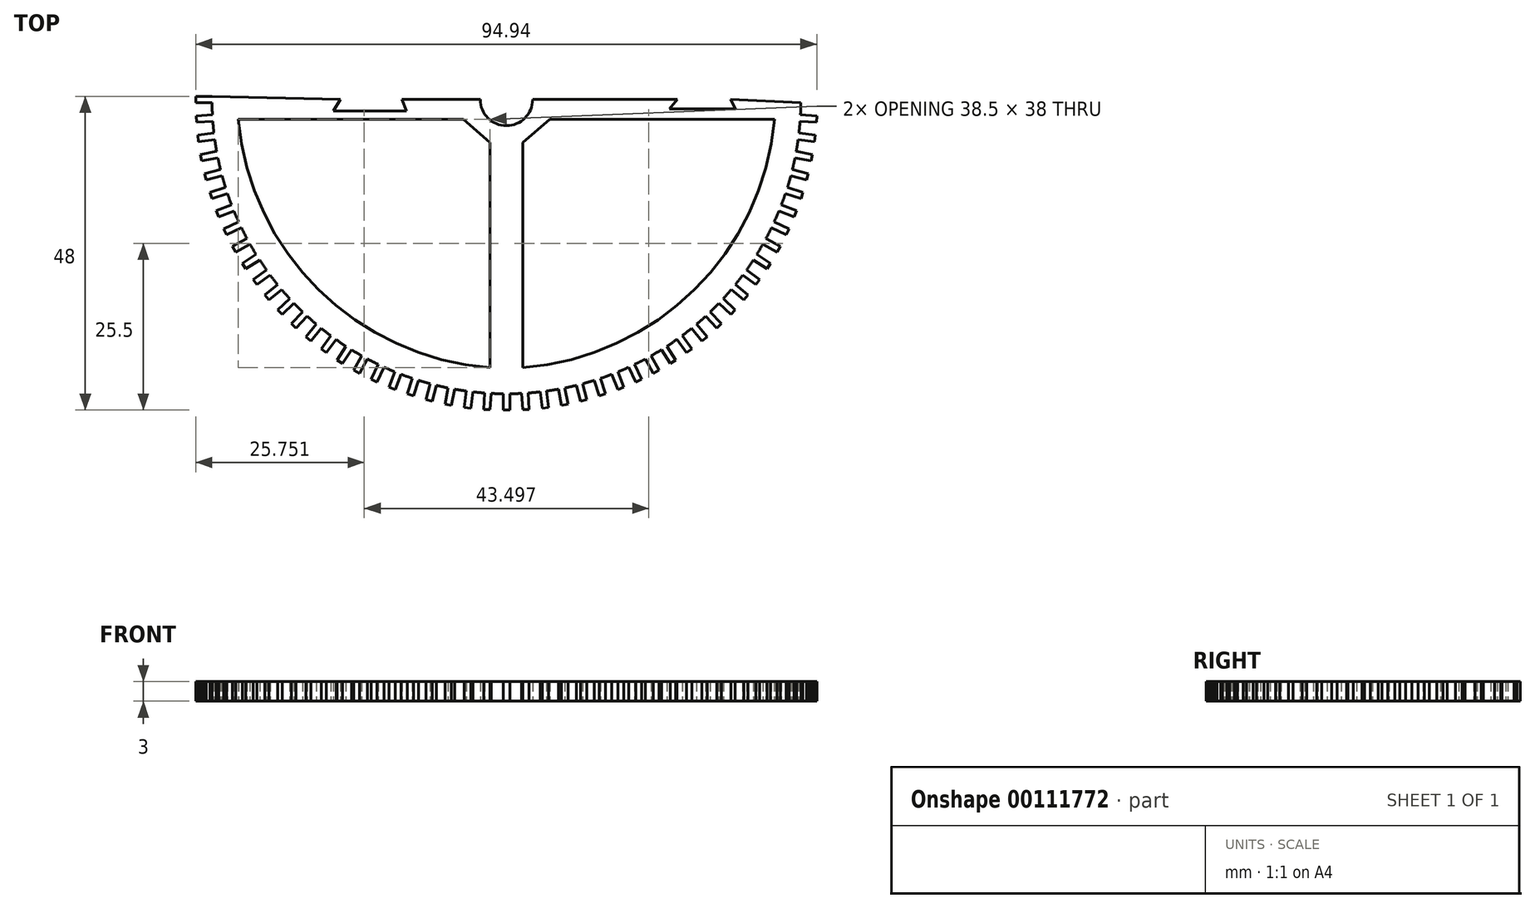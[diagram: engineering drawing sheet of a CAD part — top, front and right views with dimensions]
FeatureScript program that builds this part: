
annotation { "Feature Type Name" : "Feature", "Feature Type Description" : "" }
export const myFeature = defineFeature(function(context is Context, id is Id, definition is map)
    precondition{}
    {
        {
            var Q0;
            Q0=qCreatedBy(makeId("Top.planeOp"),FACE);
            var sketch = newSketch(context, id + "F0", { "sketchPlane" : qUnion([Q0])});
            skArc(sketch, "E0", {"start": v(-45, 0.5) * mm, "mid": v(-0.5, -45) * mm, "end": v(45, -0.5) * mm});
            skLineSegment(sketch, "E1.2.25.0", {"start": v(-47.5, 0.5) * mm, "end": v(-45, 0.5) * mm});
            skLineSegment(sketch, "E1.3.25.0", {"start": v(-47.5, -0.5) * mm, "end": v(-45, -0.5) * mm});
            skLineSegment(sketch, "E1.6.25.0", {"start": v(-47.5, 0) * mm, "end": v(-47.5, -0.5) * mm});
            skLineSegment(sketch, "E1.9.25.0", {"start": v(-47.5, 0) * mm, "end": v(-47.5, 0.5) * mm});
            skLineSegment(sketch, "E1.2.26.0", {"start": v(-47.44, -2.48) * mm, "end": v(-44.94, -2.33) * mm});
            skLineSegment(sketch, "E1.3.26.0", {"start": v(-47.37, -3.48) * mm, "end": v(-44.88, -3.32) * mm});
            skLineSegment(sketch, "E1.6.26.0", {"start": v(-47.4, -2.98) * mm, "end": v(-47.37, -3.48) * mm});
            skLineSegment(sketch, "E1.9.26.0", {"start": v(-47.4, -2.98) * mm, "end": v(-47.44, -2.48) * mm});
            skLineSegment(sketch, "E1.2.27.0", {"start": v(-47.19, -5.46) * mm, "end": v(-44.7, -5.14) * mm});
            skLineSegment(sketch, "E1.3.27.0", {"start": v(-47.06, -6.45) * mm, "end": v(-44.58, -6.14) * mm});
            skLineSegment(sketch, "E1.6.27.0", {"start": v(-47.13, -5.95) * mm, "end": v(-47.06, -6.45) * mm});
            skLineSegment(sketch, "E1.9.27.0", {"start": v(-47.13, -5.95) * mm, "end": v(-47.19, -5.46) * mm});
            skLineSegment(sketch, "E1.2.28.0", {"start": v(-46.75, -8.4) * mm, "end": v(-44.3, -7.94) * mm});
            skLineSegment(sketch, "E1.3.28.0", {"start": v(-46.56, -9.4) * mm, "end": v(-44.1, -8.92) * mm});
            skLineSegment(sketch, "E1.6.28.0", {"start": v(-46.66, -8.9) * mm, "end": v(-46.56, -9.4) * mm});
            skLineSegment(sketch, "E1.9.28.0", {"start": v(-46.66, -8.9) * mm, "end": v(-46.75, -8.4) * mm});
            skLineSegment(sketch, "E1.2.29.0", {"start": v(-46.13, -11.33) * mm, "end": v(-43.7, -10.7) * mm});
            skLineSegment(sketch, "E1.3.29.0", {"start": v(-45.88, -12.3) * mm, "end": v(-43.46, -11.67) * mm});
            skLineSegment(sketch, "E1.6.29.0", {"start": v(-46, -11.81) * mm, "end": v(-45.88, -12.3) * mm});
            skLineSegment(sketch, "E1.9.29.0", {"start": v(-46, -11.81) * mm, "end": v(-46.13, -11.33) * mm});
            skLineSegment(sketch, "E1.2.30.0", {"start": v(-45.33, -14.2) * mm, "end": v(-42.95, -13.43) * mm});
            skLineSegment(sketch, "E1.3.30.0", {"start": v(-45.02, -15.15) * mm, "end": v(-42.64, -14.38) * mm});
            skLineSegment(sketch, "E1.6.30.0", {"start": v(-45.18, -14.68) * mm, "end": v(-45.02, -15.15) * mm});
            skLineSegment(sketch, "E1.9.30.0", {"start": v(-45.18, -14.68) * mm, "end": v(-45.33, -14.2) * mm});
            skLineSegment(sketch, "E1.2.31.0", {"start": v(-44.35, -17.02) * mm, "end": v(-42.02, -16.1) * mm});
            skLineSegment(sketch, "E1.3.31.0", {"start": v(-43.98, -17.95) * mm, "end": v(-41.65, -17.03) * mm});
            skLineSegment(sketch, "E1.6.31.0", {"start": v(-44.16, -17.49) * mm, "end": v(-43.98, -17.95) * mm});
            skLineSegment(sketch, "E1.9.31.0", {"start": v(-44.16, -17.49) * mm, "end": v(-44.35, -17.02) * mm});
            skLineSegment(sketch, "E1.2.32.0", {"start": v(-43.2, -19.77) * mm, "end": v(-40.93, -18.7) * mm});
            skLineSegment(sketch, "E1.3.32.0", {"start": v(-42.77, -20.68) * mm, "end": v(-40.5, -19.61) * mm});
            skLineSegment(sketch, "E1.6.32.0", {"start": v(-42.98, -20.22) * mm, "end": v(-42.77, -20.68) * mm});
            skLineSegment(sketch, "E1.9.32.0", {"start": v(-42.98, -20.22) * mm, "end": v(-43.2, -19.77) * mm});
            skLineSegment(sketch, "E1.2.33.0", {"start": v(-41.87, -22.45) * mm, "end": v(-39.67, -21.24) * mm});
            skLineSegment(sketch, "E1.3.33.0", {"start": v(-41.38, -23.32) * mm, "end": v(-39.2, -22.12) * mm});
            skLineSegment(sketch, "E1.6.33.0", {"start": v(-41.62, -22.88) * mm, "end": v(-41.38, -23.32) * mm});
            skLineSegment(sketch, "E1.9.33.0", {"start": v(-41.62, -22.88) * mm, "end": v(-41.87, -22.45) * mm});
            skLineSegment(sketch, "E1.2.34.0", {"start": v(-40.37, -25.03) * mm, "end": v(-38.26, -23.69) * mm});
            skLineSegment(sketch, "E1.3.34.0", {"start": v(-39.84, -25.87) * mm, "end": v(-37.72, -24.53) * mm});
            skLineSegment(sketch, "E1.6.34.0", {"start": v(-40.1, -25.45) * mm, "end": v(-39.84, -25.87) * mm});
            skLineSegment(sketch, "E1.9.34.0", {"start": v(-40.1, -25.45) * mm, "end": v(-40.37, -25.03) * mm});
            skLineSegment(sketch, "E1.2.35.0", {"start": v(-38.72, -27.52) * mm, "end": v(-36.7, -26.04) * mm});
            skLineSegment(sketch, "E1.3.35.0", {"start": v(-38.13, -28.32) * mm, "end": v(-36.1, -26.85) * mm});
            skLineSegment(sketch, "E1.6.35.0", {"start": v(-38.43, -27.92) * mm, "end": v(-38.13, -28.32) * mm});
            skLineSegment(sketch, "E1.9.35.0", {"start": v(-38.43, -27.92) * mm, "end": v(-38.72, -27.52) * mm});
            skLineSegment(sketch, "E1.2.36.0", {"start": v(-36.92, -29.9) * mm, "end": v(-34.99, -28.3) * mm});
            skLineSegment(sketch, "E1.3.36.0", {"start": v(-36.28, -30.66) * mm, "end": v(-34.35, -29.07) * mm});
            skLineSegment(sketch, "E1.6.36.0", {"start": v(-36.6, -30.28) * mm, "end": v(-36.28, -30.66) * mm});
            skLineSegment(sketch, "E1.9.36.0", {"start": v(-36.6, -30.28) * mm, "end": v(-36.92, -29.9) * mm});
            skLineSegment(sketch, "E1.2.37.0", {"start": v(-34.97, -32.15) * mm, "end": v(-33.14, -30.44) * mm});
            skLineSegment(sketch, "E1.3.37.0", {"start": v(-34.28, -32.88) * mm, "end": v(-32.46, -31.17) * mm});
            skLineSegment(sketch, "E1.6.37.0", {"start": v(-34.63, -32.52) * mm, "end": v(-34.28, -32.88) * mm});
            skLineSegment(sketch, "E1.9.37.0", {"start": v(-34.63, -32.52) * mm, "end": v(-34.97, -32.15) * mm});
            skLineSegment(sketch, "E1.2.38.0", {"start": v(-32.88, -34.28) * mm, "end": v(-31.17, -32.46) * mm});
            skLineSegment(sketch, "E1.3.38.0", {"start": v(-32.15, -34.97) * mm, "end": v(-30.44, -33.14) * mm});
            skLineSegment(sketch, "E1.6.38.0", {"start": v(-32.52, -34.63) * mm, "end": v(-32.15, -34.97) * mm});
            skLineSegment(sketch, "E1.9.38.0", {"start": v(-32.52, -34.63) * mm, "end": v(-32.88, -34.28) * mm});
            skLineSegment(sketch, "E1.2.39.0", {"start": v(-30.66, -36.28) * mm, "end": v(-29.07, -34.35) * mm});
            skLineSegment(sketch, "E1.3.39.0", {"start": v(-29.9, -36.92) * mm, "end": v(-28.3, -34.99) * mm});
            skLineSegment(sketch, "E1.6.39.0", {"start": v(-30.28, -36.6) * mm, "end": v(-29.9, -36.92) * mm});
            skLineSegment(sketch, "E1.9.39.0", {"start": v(-30.28, -36.6) * mm, "end": v(-30.66, -36.28) * mm});
            skLineSegment(sketch, "E1.2.40.0", {"start": v(-28.32, -38.13) * mm, "end": v(-26.85, -36.1) * mm});
            skLineSegment(sketch, "E1.3.40.0", {"start": v(-27.52, -38.72) * mm, "end": v(-26.04, -36.7) * mm});
            skLineSegment(sketch, "E1.6.40.0", {"start": v(-27.92, -38.43) * mm, "end": v(-27.52, -38.72) * mm});
            skLineSegment(sketch, "E1.9.40.0", {"start": v(-27.92, -38.43) * mm, "end": v(-28.32, -38.13) * mm});
            skLineSegment(sketch, "E1.2.41.0", {"start": v(-25.87, -39.84) * mm, "end": v(-24.53, -37.72) * mm});
            skLineSegment(sketch, "E1.3.41.0", {"start": v(-25.03, -40.37) * mm, "end": v(-23.69, -38.26) * mm});
            skLineSegment(sketch, "E1.6.41.0", {"start": v(-25.45, -40.1) * mm, "end": v(-25.03, -40.37) * mm});
            skLineSegment(sketch, "E1.9.41.0", {"start": v(-25.45, -40.1) * mm, "end": v(-25.87, -39.84) * mm});
            skLineSegment(sketch, "E1.2.42.0", {"start": v(-23.32, -41.38) * mm, "end": v(-22.12, -39.2) * mm});
            skLineSegment(sketch, "E1.3.42.0", {"start": v(-22.45, -41.87) * mm, "end": v(-21.24, -39.67) * mm});
            skLineSegment(sketch, "E1.6.42.0", {"start": v(-22.88, -41.62) * mm, "end": v(-22.45, -41.87) * mm});
            skLineSegment(sketch, "E1.9.42.0", {"start": v(-22.88, -41.62) * mm, "end": v(-23.32, -41.38) * mm});
            skLineSegment(sketch, "E1.2.43.0", {"start": v(-20.68, -42.77) * mm, "end": v(-19.61, -40.5) * mm});
            skLineSegment(sketch, "E1.3.43.0", {"start": v(-19.77, -43.2) * mm, "end": v(-18.7, -40.93) * mm});
            skLineSegment(sketch, "E1.6.43.0", {"start": v(-20.22, -42.98) * mm, "end": v(-19.77, -43.2) * mm});
            skLineSegment(sketch, "E1.9.43.0", {"start": v(-20.22, -42.98) * mm, "end": v(-20.68, -42.77) * mm});
            skLineSegment(sketch, "E1.2.44.0", {"start": v(-17.95, -43.98) * mm, "end": v(-17.03, -41.65) * mm});
            skLineSegment(sketch, "E1.3.44.0", {"start": v(-17.02, -44.35) * mm, "end": v(-16.1, -42.02) * mm});
            skLineSegment(sketch, "E1.6.44.0", {"start": v(-17.49, -44.16) * mm, "end": v(-17.02, -44.35) * mm});
            skLineSegment(sketch, "E1.9.44.0", {"start": v(-17.49, -44.16) * mm, "end": v(-17.95, -43.98) * mm});
            skLineSegment(sketch, "E1.2.45.0", {"start": v(-15.15, -45.02) * mm, "end": v(-14.38, -42.64) * mm});
            skLineSegment(sketch, "E1.3.45.0", {"start": v(-14.2, -45.33) * mm, "end": v(-13.43, -42.95) * mm});
            skLineSegment(sketch, "E1.6.45.0", {"start": v(-14.68, -45.18) * mm, "end": v(-14.2, -45.33) * mm});
            skLineSegment(sketch, "E1.9.45.0", {"start": v(-14.68, -45.18) * mm, "end": v(-15.15, -45.02) * mm});
            skLineSegment(sketch, "E1.2.46.0", {"start": v(-12.3, -45.88) * mm, "end": v(-11.67, -43.46) * mm});
            skLineSegment(sketch, "E1.3.46.0", {"start": v(-11.33, -46.13) * mm, "end": v(-10.7, -43.7) * mm});
            skLineSegment(sketch, "E1.6.46.0", {"start": v(-11.81, -46) * mm, "end": v(-11.33, -46.13) * mm});
            skLineSegment(sketch, "E1.9.46.0", {"start": v(-11.81, -46) * mm, "end": v(-12.3, -45.88) * mm});
            skLineSegment(sketch, "E1.2.47.0", {"start": v(-9.4, -46.56) * mm, "end": v(-8.92, -44.1) * mm});
            skLineSegment(sketch, "E1.3.47.0", {"start": v(-8.4, -46.75) * mm, "end": v(-7.94, -44.3) * mm});
            skLineSegment(sketch, "E1.6.47.0", {"start": v(-8.9, -46.66) * mm, "end": v(-8.4, -46.75) * mm});
            skLineSegment(sketch, "E1.9.47.0", {"start": v(-8.9, -46.66) * mm, "end": v(-9.4, -46.56) * mm});
            skLineSegment(sketch, "E1.2.48.0", {"start": v(-6.45, -47.06) * mm, "end": v(-6.14, -44.58) * mm});
            skLineSegment(sketch, "E1.3.48.0", {"start": v(-5.46, -47.19) * mm, "end": v(-5.14, -44.7) * mm});
            skLineSegment(sketch, "E1.6.48.0", {"start": v(-5.95, -47.13) * mm, "end": v(-5.46, -47.19) * mm});
            skLineSegment(sketch, "E1.9.48.0", {"start": v(-5.95, -47.13) * mm, "end": v(-6.45, -47.06) * mm});
            skLineSegment(sketch, "E1.2.49.0", {"start": v(-3.48, -47.37) * mm, "end": v(-3.32, -44.88) * mm});
            skLineSegment(sketch, "E1.3.49.0", {"start": v(-2.48, -47.44) * mm, "end": v(-2.33, -44.94) * mm});
            skLineSegment(sketch, "E1.6.49.0", {"start": v(-2.98, -47.4) * mm, "end": v(-2.48, -47.44) * mm});
            skLineSegment(sketch, "E1.9.49.0", {"start": v(-2.98, -47.4) * mm, "end": v(-3.48, -47.37) * mm});
            skLineSegment(sketch, "E1.2.50.0", {"start": v(-0.5, -47.5) * mm, "end": v(-0.5, -45) * mm});
            skLineSegment(sketch, "E1.3.50.0", {"start": v(0.5, -47.5) * mm, "end": v(0.5, -45) * mm});
            skLineSegment(sketch, "E1.6.50.0", {"start": v(0, -47.5) * mm, "end": v(0.5, -47.5) * mm});
            skLineSegment(sketch, "E1.9.50.0", {"start": v(0, -47.5) * mm, "end": v(-0.5, -47.5) * mm});
            skLineSegment(sketch, "E1.2.51.0", {"start": v(2.48, -47.44) * mm, "end": v(2.33, -44.94) * mm});
            skLineSegment(sketch, "E1.3.51.0", {"start": v(3.48, -47.37) * mm, "end": v(3.32, -44.88) * mm});
            skLineSegment(sketch, "E1.6.51.0", {"start": v(2.98, -47.4) * mm, "end": v(3.48, -47.37) * mm});
            skLineSegment(sketch, "E1.9.51.0", {"start": v(2.98, -47.4) * mm, "end": v(2.48, -47.44) * mm});
            skLineSegment(sketch, "E1.2.52.0", {"start": v(5.46, -47.19) * mm, "end": v(5.14, -44.7) * mm});
            skLineSegment(sketch, "E1.3.52.0", {"start": v(6.45, -47.06) * mm, "end": v(6.14, -44.58) * mm});
            skLineSegment(sketch, "E1.6.52.0", {"start": v(5.95, -47.13) * mm, "end": v(6.45, -47.06) * mm});
            skLineSegment(sketch, "E1.9.52.0", {"start": v(5.95, -47.13) * mm, "end": v(5.46, -47.19) * mm});
            skLineSegment(sketch, "E1.2.53.0", {"start": v(8.4, -46.75) * mm, "end": v(7.94, -44.3) * mm});
            skLineSegment(sketch, "E1.3.53.0", {"start": v(9.4, -46.56) * mm, "end": v(8.92, -44.1) * mm});
            skLineSegment(sketch, "E1.6.53.0", {"start": v(8.9, -46.66) * mm, "end": v(9.4, -46.56) * mm});
            skLineSegment(sketch, "E1.9.53.0", {"start": v(8.9, -46.66) * mm, "end": v(8.4, -46.75) * mm});
            skLineSegment(sketch, "E1.2.54.0", {"start": v(11.33, -46.13) * mm, "end": v(10.7, -43.7) * mm});
            skLineSegment(sketch, "E1.3.54.0", {"start": v(12.3, -45.88) * mm, "end": v(11.67, -43.46) * mm});
            skLineSegment(sketch, "E1.6.54.0", {"start": v(11.81, -46) * mm, "end": v(12.3, -45.88) * mm});
            skLineSegment(sketch, "E1.9.54.0", {"start": v(11.81, -46) * mm, "end": v(11.33, -46.13) * mm});
            skLineSegment(sketch, "E1.2.55.0", {"start": v(14.2, -45.33) * mm, "end": v(13.43, -42.95) * mm});
            skLineSegment(sketch, "E1.3.55.0", {"start": v(15.15, -45.02) * mm, "end": v(14.38, -42.64) * mm});
            skLineSegment(sketch, "E1.6.55.0", {"start": v(14.68, -45.18) * mm, "end": v(15.15, -45.02) * mm});
            skLineSegment(sketch, "E1.9.55.0", {"start": v(14.68, -45.18) * mm, "end": v(14.2, -45.33) * mm});
            skLineSegment(sketch, "E1.2.56.0", {"start": v(17.02, -44.35) * mm, "end": v(16.1, -42.02) * mm});
            skLineSegment(sketch, "E1.3.56.0", {"start": v(17.95, -43.98) * mm, "end": v(17.03, -41.65) * mm});
            skLineSegment(sketch, "E1.6.56.0", {"start": v(17.49, -44.16) * mm, "end": v(17.95, -43.98) * mm});
            skLineSegment(sketch, "E1.9.56.0", {"start": v(17.49, -44.16) * mm, "end": v(17.02, -44.35) * mm});
            skLineSegment(sketch, "E1.2.57.0", {"start": v(19.77, -43.2) * mm, "end": v(18.7, -40.93) * mm});
            skLineSegment(sketch, "E1.3.57.0", {"start": v(20.68, -42.77) * mm, "end": v(19.61, -40.5) * mm});
            skLineSegment(sketch, "E1.6.57.0", {"start": v(20.22, -42.98) * mm, "end": v(20.68, -42.77) * mm});
            skLineSegment(sketch, "E1.9.57.0", {"start": v(20.22, -42.98) * mm, "end": v(19.77, -43.2) * mm});
            skLineSegment(sketch, "E1.2.58.0", {"start": v(22.45, -41.87) * mm, "end": v(21.24, -39.67) * mm});
            skLineSegment(sketch, "E1.3.58.0", {"start": v(23.32, -41.38) * mm, "end": v(22.12, -39.2) * mm});
            skLineSegment(sketch, "E1.6.58.0", {"start": v(22.88, -41.62) * mm, "end": v(23.32, -41.38) * mm});
            skLineSegment(sketch, "E1.9.58.0", {"start": v(22.88, -41.62) * mm, "end": v(22.45, -41.87) * mm});
            skLineSegment(sketch, "E1.2.59.0", {"start": v(25.03, -40.37) * mm, "end": v(23.69, -38.26) * mm});
            skLineSegment(sketch, "E1.3.59.0", {"start": v(25.87, -39.84) * mm, "end": v(24.53, -37.72) * mm});
            skLineSegment(sketch, "E1.6.59.0", {"start": v(25.45, -40.1) * mm, "end": v(25.87, -39.84) * mm});
            skLineSegment(sketch, "E1.9.59.0", {"start": v(25.45, -40.1) * mm, "end": v(25.03, -40.37) * mm});
            skLineSegment(sketch, "E1.2.60.0", {"start": v(27.52, -38.72) * mm, "end": v(26.04, -36.7) * mm});
            skLineSegment(sketch, "E1.3.60.0", {"start": v(28.32, -38.13) * mm, "end": v(26.85, -36.1) * mm});
            skLineSegment(sketch, "E1.6.60.0", {"start": v(27.92, -38.43) * mm, "end": v(28.32, -38.13) * mm});
            skLineSegment(sketch, "E1.9.60.0", {"start": v(27.92, -38.43) * mm, "end": v(27.52, -38.72) * mm});
            skLineSegment(sketch, "E1.2.61.0", {"start": v(29.9, -36.92) * mm, "end": v(28.3, -34.99) * mm});
            skLineSegment(sketch, "E1.3.61.0", {"start": v(30.66, -36.28) * mm, "end": v(29.07, -34.35) * mm});
            skLineSegment(sketch, "E1.6.61.0", {"start": v(30.28, -36.6) * mm, "end": v(30.66, -36.28) * mm});
            skLineSegment(sketch, "E1.9.61.0", {"start": v(30.28, -36.6) * mm, "end": v(29.9, -36.92) * mm});
            skLineSegment(sketch, "E1.2.62.0", {"start": v(32.15, -34.97) * mm, "end": v(30.44, -33.14) * mm});
            skLineSegment(sketch, "E1.3.62.0", {"start": v(32.88, -34.28) * mm, "end": v(31.17, -32.46) * mm});
            skLineSegment(sketch, "E1.6.62.0", {"start": v(32.52, -34.63) * mm, "end": v(32.88, -34.28) * mm});
            skLineSegment(sketch, "E1.9.62.0", {"start": v(32.52, -34.63) * mm, "end": v(32.15, -34.97) * mm});
            skLineSegment(sketch, "E1.2.63.0", {"start": v(34.28, -32.88) * mm, "end": v(32.46, -31.17) * mm});
            skLineSegment(sketch, "E1.3.63.0", {"start": v(34.97, -32.15) * mm, "end": v(33.14, -30.44) * mm});
            skLineSegment(sketch, "E1.6.63.0", {"start": v(34.63, -32.52) * mm, "end": v(34.97, -32.15) * mm});
            skLineSegment(sketch, "E1.9.63.0", {"start": v(34.63, -32.52) * mm, "end": v(34.28, -32.88) * mm});
            skLineSegment(sketch, "E1.2.64.0", {"start": v(36.28, -30.66) * mm, "end": v(34.35, -29.07) * mm});
            skLineSegment(sketch, "E1.3.64.0", {"start": v(36.92, -29.9) * mm, "end": v(34.99, -28.3) * mm});
            skLineSegment(sketch, "E1.6.64.0", {"start": v(36.6, -30.28) * mm, "end": v(36.92, -29.9) * mm});
            skLineSegment(sketch, "E1.9.64.0", {"start": v(36.6, -30.28) * mm, "end": v(36.28, -30.66) * mm});
            skLineSegment(sketch, "E1.2.65.0", {"start": v(38.13, -28.32) * mm, "end": v(36.1, -26.85) * mm});
            skLineSegment(sketch, "E1.3.65.0", {"start": v(38.72, -27.52) * mm, "end": v(36.7, -26.04) * mm});
            skLineSegment(sketch, "E1.6.65.0", {"start": v(38.43, -27.92) * mm, "end": v(38.72, -27.52) * mm});
            skLineSegment(sketch, "E1.9.65.0", {"start": v(38.43, -27.92) * mm, "end": v(38.13, -28.32) * mm});
            skLineSegment(sketch, "E1.2.66.0", {"start": v(39.84, -25.87) * mm, "end": v(37.72, -24.53) * mm});
            skLineSegment(sketch, "E1.3.66.0", {"start": v(40.37, -25.03) * mm, "end": v(38.26, -23.69) * mm});
            skLineSegment(sketch, "E1.6.66.0", {"start": v(40.1, -25.45) * mm, "end": v(40.37, -25.03) * mm});
            skLineSegment(sketch, "E1.9.66.0", {"start": v(40.1, -25.45) * mm, "end": v(39.84, -25.87) * mm});
            skLineSegment(sketch, "E1.2.67.0", {"start": v(41.38, -23.32) * mm, "end": v(39.2, -22.12) * mm});
            skLineSegment(sketch, "E1.3.67.0", {"start": v(41.87, -22.45) * mm, "end": v(39.67, -21.24) * mm});
            skLineSegment(sketch, "E1.6.67.0", {"start": v(41.62, -22.88) * mm, "end": v(41.87, -22.45) * mm});
            skLineSegment(sketch, "E1.9.67.0", {"start": v(41.62, -22.88) * mm, "end": v(41.38, -23.32) * mm});
            skLineSegment(sketch, "E1.2.68.0", {"start": v(42.77, -20.68) * mm, "end": v(40.5, -19.61) * mm});
            skLineSegment(sketch, "E1.3.68.0", {"start": v(43.2, -19.77) * mm, "end": v(40.93, -18.7) * mm});
            skLineSegment(sketch, "E1.6.68.0", {"start": v(42.98, -20.22) * mm, "end": v(43.2, -19.77) * mm});
            skLineSegment(sketch, "E1.9.68.0", {"start": v(42.98, -20.22) * mm, "end": v(42.77, -20.68) * mm});
            skLineSegment(sketch, "E1.2.69.0", {"start": v(43.98, -17.95) * mm, "end": v(41.65, -17.03) * mm});
            skLineSegment(sketch, "E1.3.69.0", {"start": v(44.35, -17.02) * mm, "end": v(42.02, -16.1) * mm});
            skLineSegment(sketch, "E1.6.69.0", {"start": v(44.16, -17.49) * mm, "end": v(44.35, -17.02) * mm});
            skLineSegment(sketch, "E1.9.69.0", {"start": v(44.16, -17.49) * mm, "end": v(43.98, -17.95) * mm});
            skLineSegment(sketch, "E1.2.70.0", {"start": v(45.02, -15.15) * mm, "end": v(42.64, -14.38) * mm});
            skLineSegment(sketch, "E1.3.70.0", {"start": v(45.33, -14.2) * mm, "end": v(42.95, -13.43) * mm});
            skLineSegment(sketch, "E1.6.70.0", {"start": v(45.18, -14.68) * mm, "end": v(45.33, -14.2) * mm});
            skLineSegment(sketch, "E1.9.70.0", {"start": v(45.18, -14.68) * mm, "end": v(45.02, -15.15) * mm});
            skLineSegment(sketch, "E1.2.71.0", {"start": v(45.88, -12.3) * mm, "end": v(43.46, -11.67) * mm});
            skLineSegment(sketch, "E1.3.71.0", {"start": v(46.13, -11.33) * mm, "end": v(43.7, -10.7) * mm});
            skLineSegment(sketch, "E1.6.71.0", {"start": v(46, -11.81) * mm, "end": v(46.13, -11.33) * mm});
            skLineSegment(sketch, "E1.9.71.0", {"start": v(46, -11.81) * mm, "end": v(45.88, -12.3) * mm});
            skLineSegment(sketch, "E1.2.72.0", {"start": v(46.56, -9.4) * mm, "end": v(44.1, -8.92) * mm});
            skLineSegment(sketch, "E1.3.72.0", {"start": v(46.75, -8.4) * mm, "end": v(44.3, -7.94) * mm});
            skLineSegment(sketch, "E1.6.72.0", {"start": v(46.66, -8.9) * mm, "end": v(46.75, -8.4) * mm});
            skLineSegment(sketch, "E1.9.72.0", {"start": v(46.66, -8.9) * mm, "end": v(46.56, -9.4) * mm});
            skLineSegment(sketch, "E1.2.73.0", {"start": v(47.06, -6.45) * mm, "end": v(44.58, -6.14) * mm});
            skLineSegment(sketch, "E1.3.73.0", {"start": v(47.19, -5.46) * mm, "end": v(44.7, -5.14) * mm});
            skLineSegment(sketch, "E1.6.73.0", {"start": v(47.13, -5.95) * mm, "end": v(47.19, -5.46) * mm});
            skLineSegment(sketch, "E1.9.73.0", {"start": v(47.13, -5.95) * mm, "end": v(47.06, -6.45) * mm});
            skLineSegment(sketch, "E1.2.74.0", {"start": v(47.37, -3.48) * mm, "end": v(44.88, -3.32) * mm});
            skLineSegment(sketch, "E1.3.74.0", {"start": v(47.44, -2.48) * mm, "end": v(44.94, -2.33) * mm});
            skLineSegment(sketch, "E1.6.74.0", {"start": v(47.4, -2.98) * mm, "end": v(47.44, -2.48) * mm});
            skLineSegment(sketch, "E1.9.74.0", {"start": v(47.4, -2.98) * mm, "end": v(47.37, -3.48) * mm});
            skLineSegment(sketch, "E2.MirrorCS", {"start": v(-6.6, -3) * mm, "end": v(-41, -3) * mm});
            skLineSegment(sketch, "E3.MirrorCS", {"start": v(-2.5, -6.6) * mm, "end": v(-6.6, -3) * mm});
            skLineSegment(sketch, "E4.MirrorCS", {"start": v(-2.5, -6.6) * mm, "end": v(-2.5, -41) * mm});
            skArc(sketch, "E5.MirrorCS", {"start": v(-41, -3) * mm, "mid": v(-28.72, -29.07) * mm, "end": v(-2.5, -41) * mm});
            skLineSegment(sketch, "E6.MirrorCS", {"start": v(2.5, -6.6) * mm, "end": v(2.5, -41) * mm});
            skLineSegment(sketch, "E7.MirrorCS", {"start": v(2.5, -6.6) * mm, "end": v(6.6, -3) * mm});
            skLineSegment(sketch, "E8.MirrorCS", {"start": v(6.6, -3) * mm, "end": v(41, -3) * mm});
            skArc(sketch, "E9.MirrorCS", {"start": v(41, -3) * mm, "mid": v(28.72, -29.07) * mm, "end": v(2.5, -41) * mm});
            skArc(sketch, "E10", {"start": v(-4, 0) * mm, "mid": v(0, -4) * mm, "end": v(4, 0) * mm});
            skLineSegment(sketch, "E11", {"start": v(-4, 0) * mm, "end": v(-16, 0) * mm});
            skLineSegment(sketch, "E12", {"start": v(-16, 0) * mm, "end": v(-15.27, -1.74) * mm});
            skLineSegment(sketch, "E13", {"start": v(-15.27, -1.74) * mm, "end": v(-26.47, -1.74) * mm});
            skLineSegment(sketch, "E14", {"start": v(-45, 0.5) * mm, "end": v(-25.37, 0) * mm});
            skLineSegment(sketch, "E15", {"start": v(-25.37, 0) * mm, "end": v(-26.47, -1.74) * mm});
            skLineSegment(sketch, "E16", {"start": v(45, -0.5) * mm, "end": v(34.22, 0) * mm});
            skLineSegment(sketch, "E17", {"start": v(34.22, 0) * mm, "end": v(35.03, -1.4) * mm});
            skLineSegment(sketch, "E18", {"start": v(35.03, -1.4) * mm, "end": v(24.89, -1.4) * mm});
            skLineSegment(sketch, "E19", {"start": v(24.89, -1.4) * mm, "end": v(26.1, 0) * mm});
            skLineSegment(sketch, "E20", {"start": v(26.1, 0) * mm, "end": v(4, 0) * mm});
            skSolve(sketch);
        }
        {
            var Q0;
            Q0=qSketchRegion(id+"F0",true);
            extrude(context, id + "F1", {"entities" : qUnion([Q0]), "depth" : 3 * mm});
        }
    });
